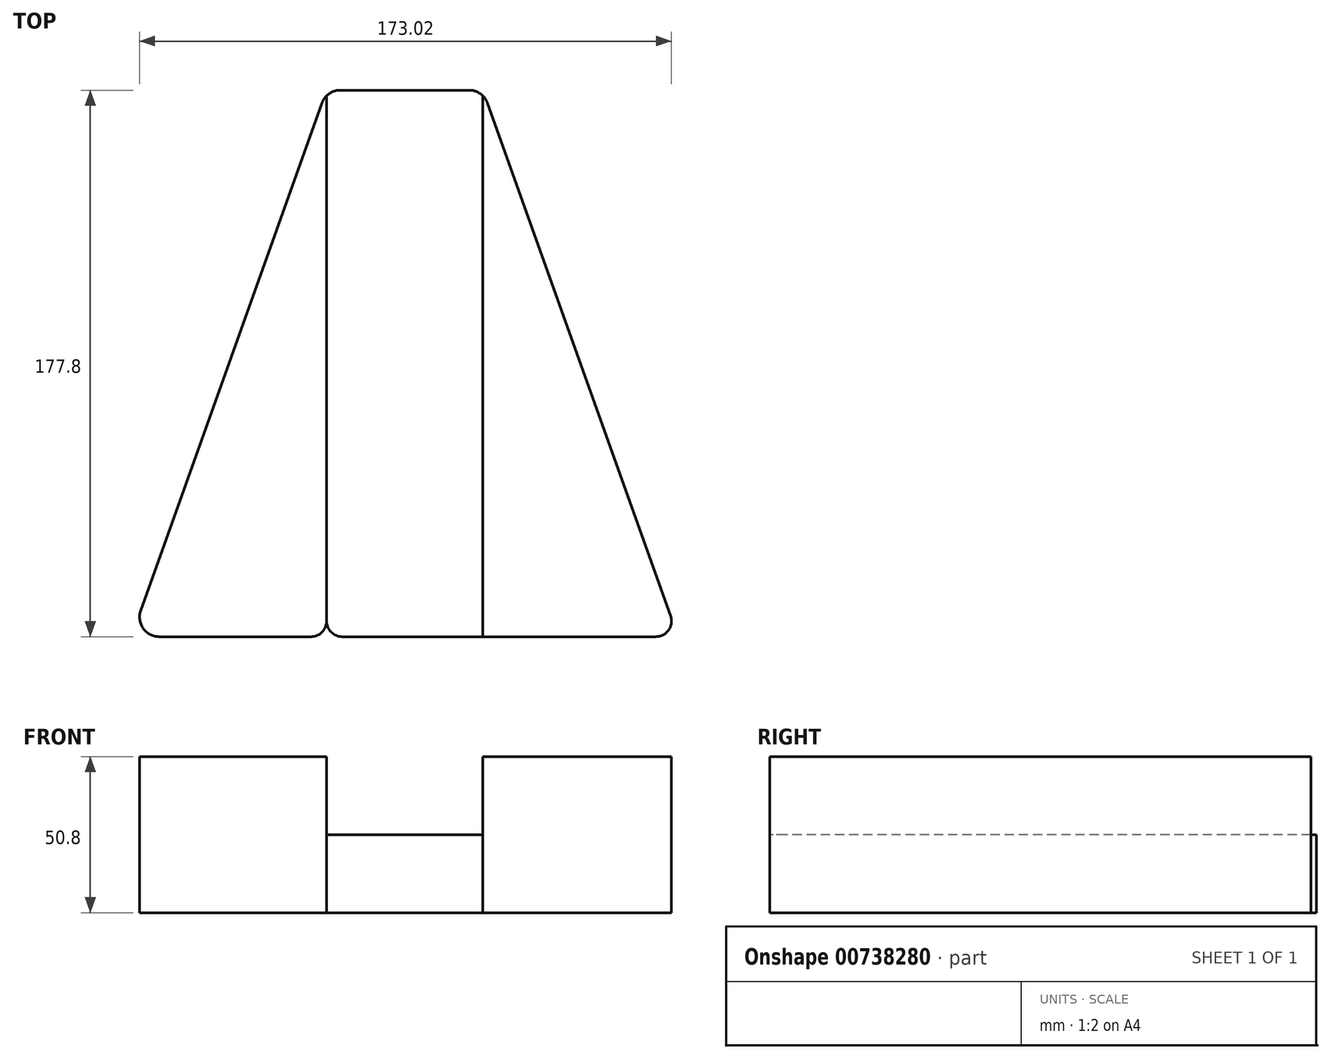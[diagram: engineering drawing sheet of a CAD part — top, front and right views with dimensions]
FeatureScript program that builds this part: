
annotation { "Feature Type Name" : "Feature", "Feature Type Description" : "" }
export const myFeature = defineFeature(function(context is Context, id is Id, definition is map)
    precondition{}
    {
        {
            var Q0;
            Q0=qCreatedBy(makeId("Top.planeOp"),FACE);
            var sketch = newSketch(context, id + "F0", { "sketchPlane" : qUnion([Q0])});
            skLineSegment(sketch, "E0", {"start": v(-31.2, 167.18) * mm, "end": v(10.65, 167.18) * mm});
            skLineSegment(sketch, "E1", {"start": v(16.63, 162.97) * mm, "end": v(78.62, -10.62) * mm});
            skLineSegment(sketch, "E2", {"start": v(78.62, -10.62) * mm, "end": v(-99.18, -10.62) * mm});
            skLineSegment(sketch, "E3", {"start": v(-99.18, -10.62) * mm, "end": v(-37.18, 162.97) * mm});
            skLineSegment(sketch, "E4", {"start": v(-35.68, 167.18) * mm, "end": v(-35.68, -10.62) * mm});
            skLineSegment(sketch, "E5", {"start": v(15.12, 167.18) * mm, "end": v(15.12, -10.62) * mm});
            skPoint(sketch, "E6.visualSharp", {"position": v(15.12, 167.18) * mm});
            skArc(sketch, "E6.filletArc", {"start": v(16.63, 162.97) * mm, "mid": v(14.3, 166.02) * mm, "end": v(10.65, 167.18) * mm});
            skPoint(sketch, "E7.visualSharp", {"position": v(-35.68, 167.18) * mm});
            skArc(sketch, "E7.filletArc", {"start": v(-31.2, 167.18) * mm, "mid": v(-34.86, 166.02) * mm, "end": v(-37.18, 162.97) * mm});
            skSolve(sketch);
        }
        {
            var Q0;
            {var subQ0=sQuery(id+"F0.wireOp",EDGE,"E3");Q0=makeQuery(id+"F0.imprint","IMPRINT",FACE,{"disambiguationData":[TD([[makeQuery(id+"F0.imprint","IMPRINT",EDGE,{"derivedFrom":subQ0}),-1.0]])]});}
            var Q1;
            {var subQ0=sQuery(id+"F0.wireOp",EDGE,"E1");Q1=makeQuery(id+"F0.imprint","IMPRINT",FACE,{"disambiguationData":[TD([[makeQuery(id+"F0.imprint","IMPRINT",EDGE,{"derivedFrom":subQ0}),-1.0]])]});}
            extrude(context, id + "F1", {"entities" : qUnion([Q0, Q1]), "depth" : 50.8 * mm, "offsetDistance" : 25.4 * mm});
        }
        {
            var Q0;
            Q0=makeQuery(id+"F0.imprint","IMPRINT",FACE,{"disambiguationData":[TD([[makeQuery(id+"F0.imprint","IMPRINT",EDGE,{"derivedFrom":sQuery(id+"F0.wireOp",EDGE,"E0")}),-1.0]])]});
            extrude(context, id + "F2", {"entities" : qUnion([Q0]), "depth" : 25.4 * mm, "offsetDistance" : 25.4 * mm});
        }
        {
            var Q0;
            Q0=makeQuery(id+"F1.opExtrude","SWEPT_EDGE",EDGE,{"disambiguationData":[OSD([sQuery(id+"F0.wireOp",EDGE,"E2"),sQuery(id+"F0.wireOp",EDGE,"E3")])]});
            fillet(context, id + "F3", {"entities" : qUnion([Q0]), "radius" : 6.35 * mm, "tangentPropagation" : true, "allowEdgeOverflow" : false});
        }
        {
            var Q0;
            Q0=makeQuery(id+"F1.opExtrude","SWEPT_EDGE",EDGE,{"disambiguationData":[OSD([sQuery(id+"F0.wireOp",EDGE,"E1"),sQuery(id+"F0.wireOp",EDGE,"E2")])]});
            fillet(context, id + "F4", {"entities" : qUnion([Q0]), "radius" : 5.08 * mm, "tangentPropagation" : true, "allowEdgeOverflow" : false});
        }
        {
            var Q0;
            Q0=makeQuery(id+"F1.opExtrude","SWEPT_EDGE",EDGE,{"disambiguationData":[OSD([sQuery(id+"F0.wireOp",EDGE,"E2"),sQuery(id+"F0.wireOp",EDGE,"E4")])]});
            fillet(context, id + "F5", {"entities" : qUnion([Q0]), "radius" : 5.08 * mm, "tangentPropagation" : true, "allowEdgeOverflow" : false});
        }
        {
            var Q0;
            Q0=makeQuery(id+"F2.opExtrude","SWEPT_EDGE",EDGE,{"disambiguationData":[OSD([sQuery(id+"F0.wireOp",EDGE,"E2"),sQuery(id+"F0.wireOp",EDGE,"E4")])]});
            fillet(context, id + "F6", {"entities" : qUnion([Q0]), "radius" : 5.08 * mm, "tangentPropagation" : true, "allowEdgeOverflow" : false});
        }
    });
